# Revit family: C_EGCM90_2DO_CAD_MULT_Prod
name_source: partatom
category: Detail Items
revit_build: Autodesk Revit 2015 (Build: 20140606_1530(x64)
units: mm (PartAtom-declared; Revit-internal decimal feet)

## types (4) — shared parameters
Density = 0.17 kg
Description = Concealed beam hanger
EPD = https://www.strongtie.eu
ETA / DoP = https://www.strongtie.eu
Manufacturer = Simpson Strong-Tie
Model = EGCM90
Model Disclaimer = Contact Simpson Strong-Tie Company  for more information
Model ID = 0264518491534717256550380103612535099994
Name = EGCM90
ObjectType = EGCM90
Product Material = Aluminium
Product Type = Concealed beam hanger
Reference = EGCM90
Technical datasheet = https://www.strongtie.eu
URL = www.strongtie.eu
UniClass Number = Pr_20_85_09_02
UniClass Title = Aluminium brackets

## per-type parameters (varying)
| type | _visiblefront | _visibleleft | _visibleright | _visibletop |
| SST_EGCM90_Front | Yes | No | No | No |
| SST_EGCM90_Top | No | No | No | Yes |
| SST_EGCM90_Left | No | Yes | No | No |
| SST_EGCM90_Right | No | No | Yes | No |

## geometry (parser evidence)
native form markers: Sweep x2
no freeform markers — native parametric forms only
